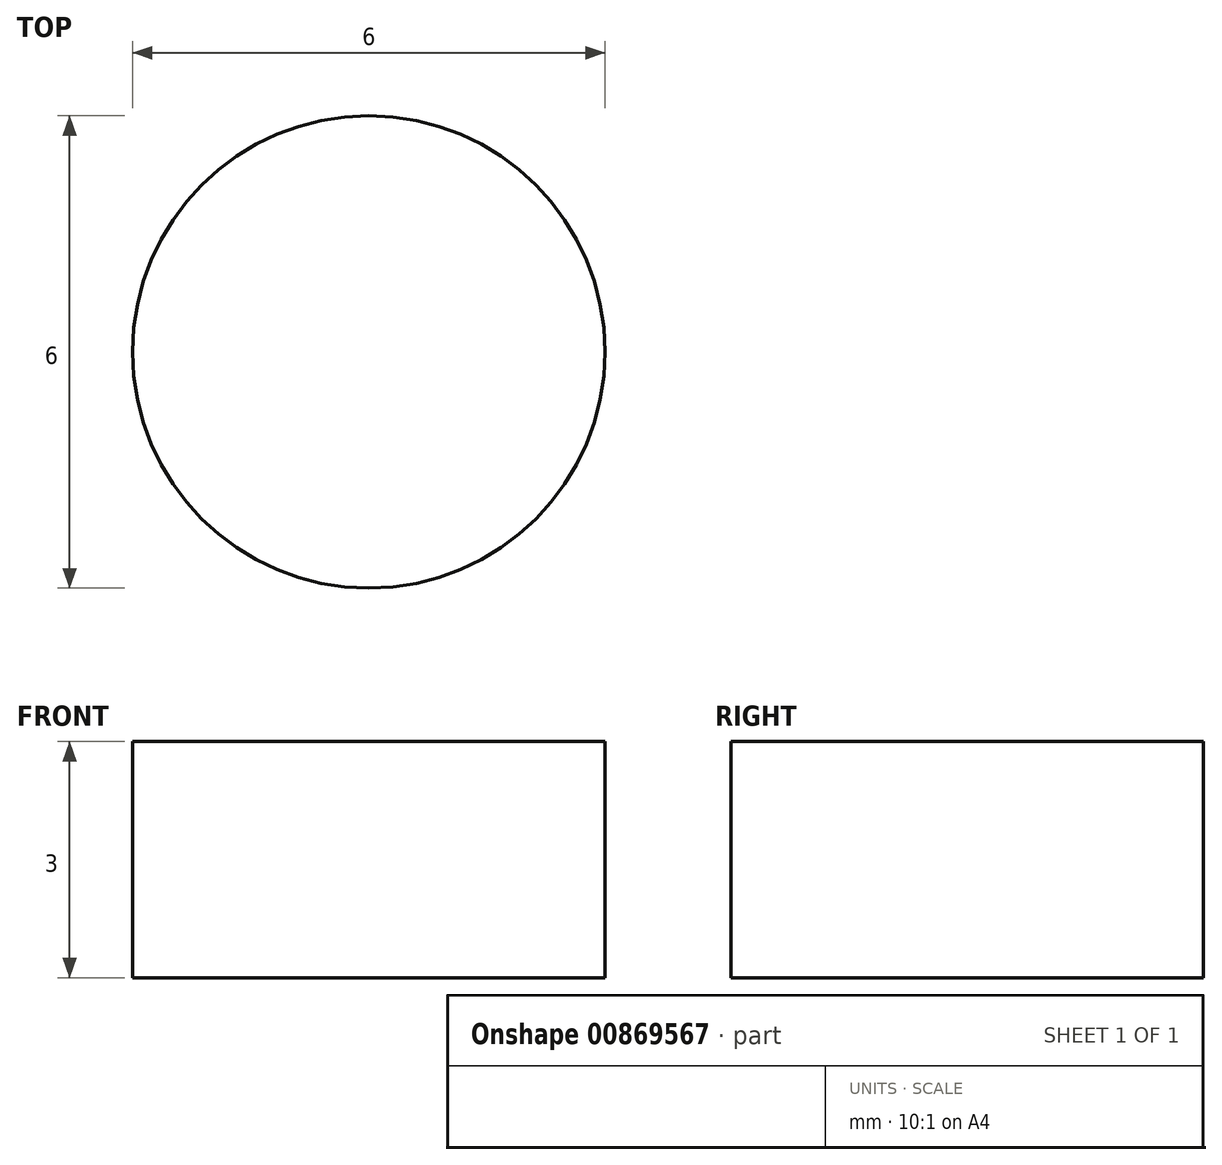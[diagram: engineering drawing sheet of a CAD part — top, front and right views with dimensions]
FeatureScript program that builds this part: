
annotation { "Feature Type Name" : "Feature", "Feature Type Description" : "" }
export const myFeature = defineFeature(function(context is Context, id is Id, definition is map)
    precondition{}
    {
        {
            var Q0;
            Q0=qCreatedBy(makeId("Top.planeOp"),FACE);
            var sketch = newSketch(context, id + "F0", { "sketchPlane" : qUnion([Q0])});
            skCircle(sketch, "E0", {"center": v(0, 0) * mm, "radius": 3 * mm});
            skSolve(sketch);
        }
        {
            var Q0;
            Q0 = qSketchRegion(id + "F0", true);
            extrude(context, id + "F1", {"entities" : qUnion([Q0]), "depth" : 3 * mm, "offsetDistance" : 25 * mm});
        }
    });
